# Revit family: FONESTAR_Altavoz_Exponencial_Exterior_EN-54
name_source: partatom
category: Dispositivos de comunicación
units: mm (PartAtom-declared; Revit-internal decimal feet)

## family parameters
Compartido = No
Corte con vacíos al cargar = No
Cota de conector redondo = Diámetro de uso
Mantener orientación de anotación = No
Punto de cálculo de habitación = No
Se basa en plano de trabajo = Sí
Siempre vertical = No
Tipo de pieza = Normal

## types (1)
- FONESTAR_Altavoz_Exponencial_Exterior_EN-54
    Altura = 122 mm  [stored 0.400262 ft]
    Base.Soporte.Espesor = 2 mm  [stored 0.00656168 ft]
    Cuerpo.Altura.Inferior = 106 mm  [stored 0.347769 ft]
    Cuerpo.Diámetro.Interior = 120 mm  [stored 0.393701 ft]
    Cuerpo.Espesor = 5 mm  [stored 0.0164042 ft]
    Cuerpo.Material = Plástico ABS - Gris RAL(7035)
    Descripción = Altavoz exponencial EN 54 con transformador de línea 100 V.
    Diámetro = 212 mm  [stored 0.695538 ft]
    Elevación por defecto = 1000 mm  [stored 3.28084 ft]
    Fabricante = FONESTAR
    Lente.Espesor = 5 mm  [stored 0.0164042 ft]
    Longitud = 280 mm  [stored 0.918635 ft]
    Modelo = FE-2010T-EN
    Modified by = XPV
    Peso = 2,1 Kg
    Potencia Acústica = 30 W RMS
    Protección IP = IP-66
    Rejilla.Espesor = 2 mm  [stored 0.00656168 ft]
    Respuesta Acústica = 340-9.000 Hz
    Reviewed by = TAG
    Soporte.Altura = 142 mm  [stored 0.465879 ft]
    Soporte.Anchura = 40 mm  [stored 0.131234 ft]
    Soporte.Espesor = 3 mm  [stored 0.00984252 ft]
    Soporte.Longitud = 124 mm  [stored 0.406824 ft]
    Soporte.Material = Plástico ABS - Gris RAL(7035)
    URL = https://fonestar.com
    URL.Product = https://fonestar.com
    Version = R0

note: [stored X ft] marks values corroborated as IEEE doubles in the binary element streams (Revit-internal decimal feet)
